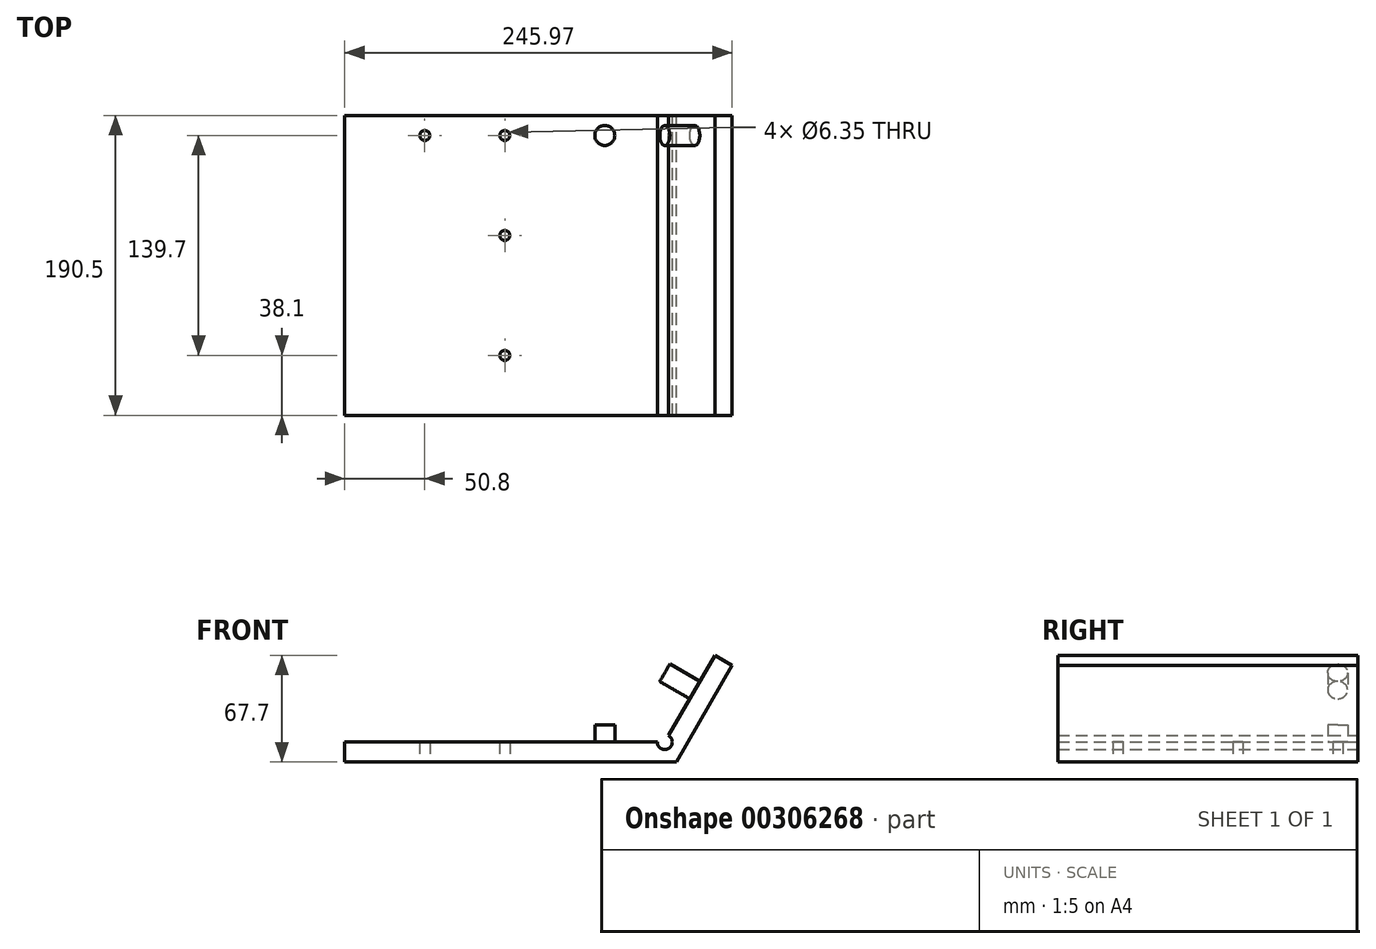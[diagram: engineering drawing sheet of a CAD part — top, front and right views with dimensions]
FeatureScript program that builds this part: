
annotation { "Feature Type Name" : "Feature", "Feature Type Description" : "" }
export const myFeature = defineFeature(function(context is Context, id is Id, definition is map)
    precondition{}
    {
        {
            var Q0;
            Q0=qCreatedBy(makeId("Front.planeOp"),FACE);
            var sketch = newSketch(context, id + "F0", { "sketchPlane" : qUnion([Q0])});
            skLineSegment(sketch, "E0.bottom", {"start": v(93.18, 6.35) * mm, "end": v(-93.18, 6.35) * mm});
            skLineSegment(sketch, "E0.top", {"start": v(105.27, -6.35) * mm, "end": v(-105.27, -6.35) * mm});
            skPoint(sketch, "E0.middle", {"position": v(0, 0) * mm});
            skLineSegment(sketch, "E1.MirrorCS", {"start": v(129.7, 61.35) * mm, "end": v(100.32, 10.47) * mm});
            skLineSegment(sketch, "E2.MirrorCS", {"start": v(140.7, 55) * mm, "end": v(129.7, 61.35) * mm});
            skLineSegment(sketch, "E3.MirrorCS", {"start": v(105.27, -6.35) * mm, "end": v(140.7, 55) * mm});
            skPoint(sketch, "E4.MirrorP", {"position": v(105.27, 6.35) * mm});
            skArc(sketch, "E5.MirrorCS", {"start": v(100.32, 10.47) * mm, "mid": v(100.32, 2.23) * mm, "end": v(93.18, 6.35) * mm});
            skLineSegment(sketch, "E6", {"start": v(-105.27, -6.35) * mm, "end": v(-105.27, 6.35) * mm});
            skLineSegment(sketch, "E7", {"start": v(-93.18, 6.35) * mm, "end": v(-105.27, 6.35) * mm});
            skSolve(sketch);
        }
        {
            var Q0;
            Q0 = qSketchRegion(id + "F0", true);
            extrude(context, id + "F1", {"entities" : qUnion([Q0]), "depth" : 190.5 * mm});
        }
        {
            var Q0;
            Q0=makeQuery(id+"F1.opExtrude","SWEPT_FACE",FACE,{"disambiguationData":[OSD([sQuery(id+"F0.wireOp",EDGE,"E0.top")])]});
            var sketch = newSketch(context, id + "F2", { "sketchPlane" : qUnion([Q0])});
            skLineSegment(sketch, "E8", {"start": v(105.27, 190.5) * mm, "end": v(-3.67, 190.5) * mm});
            skLineSegment(sketch, "E9", {"start": v(105.27, 190.5) * mm, "end": v(-54.47, 190.5) * mm});
            skLineSegment(sketch, "E10", {"start": v(-3.67, 190.5) * mm, "end": v(-3.67, 152.4) * mm});
            skLineSegment(sketch, "E11", {"start": v(-3.67, 152.4) * mm, "end": v(-3.67, 76.2) * mm});
            skLineSegment(sketch, "E12", {"start": v(-3.67, 76.2) * mm, "end": v(-3.67, 12.7) * mm});
            skLineSegment(sketch, "E13", {"start": v(-3.67, 12.7) * mm, "end": v(-54.47, 12.7) * mm});
            skPoint(sketch, "E14", {"position": v(-54.47, 12.7) * mm});
            skPoint(sketch, "E15", {"position": v(-3.67, 12.7) * mm});
            skPoint(sketch, "E16", {"position": v(-3.67, 76.2) * mm});
            skPoint(sketch, "E17", {"position": v(-3.67, 152.4) * mm});
            skSolve(sketch);
        }
        {
            var Q0;
            Q0=sQuery(id+"F2.wireOp",VERTEX,"E17");
            var Q1;
            Q1=sQuery(id+"F2.wireOp",VERTEX,"E16");
            var Q2;
            Q2=sQuery(id+"F2.wireOp",VERTEX,"E15");
            var Q3;
            Q3=sQuery(id+"F2.wireOp",VERTEX,"E14");
            var Q4;
            Q4=makeQuery(id+"F1.opExtrude","SWEPT_BODY",BODY,{"disambiguationData":[OSD([sQuery(id+"F0.wireOp",EDGE,"E0.bottom"),sQuery(id+"F0.wireOp",EDGE,"E0.top"),sQuery(id+"F0.wireOp",EDGE,"E2.MirrorCS"),sQuery(id+"F0.wireOp",EDGE,"E3.MirrorCS"),sQuery(id+"F0.wireOp",EDGE,"E1.MirrorCS"),sQuery(id+"F0.wireOp",EDGE,"E5.MirrorCS"),sQuery(id+"F0.wireOp",EDGE,"E6"),sQuery(id+"F0.wireOp",EDGE,"E7")])]});
            hole(context, id + "F3", {"style" : HoleStyle.SIMPLE, "endStyle" : HoleEndStyle.THROUGH, "holeDiameter" : 6.35 * mm, "tappedDepth" : 12.7 * mm, "tapClearance" : 3, "locations" : qUnion([Q0, Q1, Q2, Q3]), "scope" : qUnion([Q4])});
        }
        {
            var Q0;
            Q0=makeQuery(id+"F1.opExtrude","SWEPT_FACE",FACE,{"disambiguationData":[OSD([sQuery(id+"F0.wireOp",EDGE,"E0.bottom"),sQuery(id+"F0.wireOp",EDGE,"E7")])]});
            var sketch = newSketch(context, id + "F4", { "sketchPlane" : qUnion([Q0])});
            skLineSegment(sketch, "E18", {"start": v(-105.27, 0) * mm, "end": v(105.27, 0) * mm});
            skLineSegment(sketch, "E19", {"start": v(105.27, 0) * mm, "end": v(59.83, 0) * mm});
            skLineSegment(sketch, "E20", {"start": v(59.83, 0) * mm, "end": v(59.83, -12.7) * mm});
            skCircle(sketch, "E21", {"center": v(59.83, -12.7) * mm, "radius": 6.35 * mm});
            skSolve(sketch);
        }
        {
            var Q0;
            Q0 = qSketchRegion(id + "F4", true);
            extrude(context, id + "F5", {"entities" : qUnion([Q0]), "operationType" : NewBodyOperationType.ADD, "depth" : 11 * mm});
        }
        {
            var Q0;
            Q0=makeQuery(id+"F1.opExtrude","SWEPT_FACE",FACE,{"disambiguationData":[OSD([sQuery(id+"F0.wireOp",EDGE,"E1.MirrorCS")])]});
            var sketch = newSketch(context, id + "F6", { "sketchPlane" : qUnion([Q0])});
            skLineSegment(sketch, "E22", {"start": v(0, 117.98) * mm, "end": v(0, 92.58) * mm});
            skLineSegment(sketch, "E23", {"start": v(0, 92.58) * mm, "end": v(12.7, 92.58) * mm});
            skCircle(sketch, "E24", {"center": v(12.7, 92.58) * mm, "radius": 6.35 * mm});
            skSolve(sketch);
        }
        {
            var Q0;
            Q0 = qSketchRegion(id + "F6", true);
            extrude(context, id + "F7", {"entities" : qUnion([Q0]), "operationType" : NewBodyOperationType.ADD, "depth" : 22 * mm});
        }
    });
